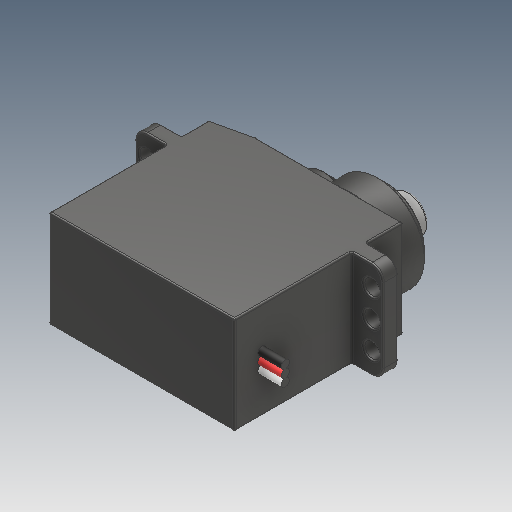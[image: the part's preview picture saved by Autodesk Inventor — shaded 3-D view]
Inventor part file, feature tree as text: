
AUTODESK INVENTOR PART (.ipt)
format: ipt  version: 2018 (Build 220112000, 112)  size: 399,872 bytes
history: native  units: mm
features: fillet x1
ambient origin geometry x8: Origin, YZ Plane, XZ Plane, XY Plane, X Axis, Y Axis, Z Axis, Center Point
bodies: Volumenkörper1 (feature_tree)
feature tree (1):
  fillet  "Congé49"  [1 undecoded]
note: 1 required parameter value undecoded (feature->parameter linkage not recoverable at this tier; creation-order binding heuristic only, values carry confidence <= 0.55)
